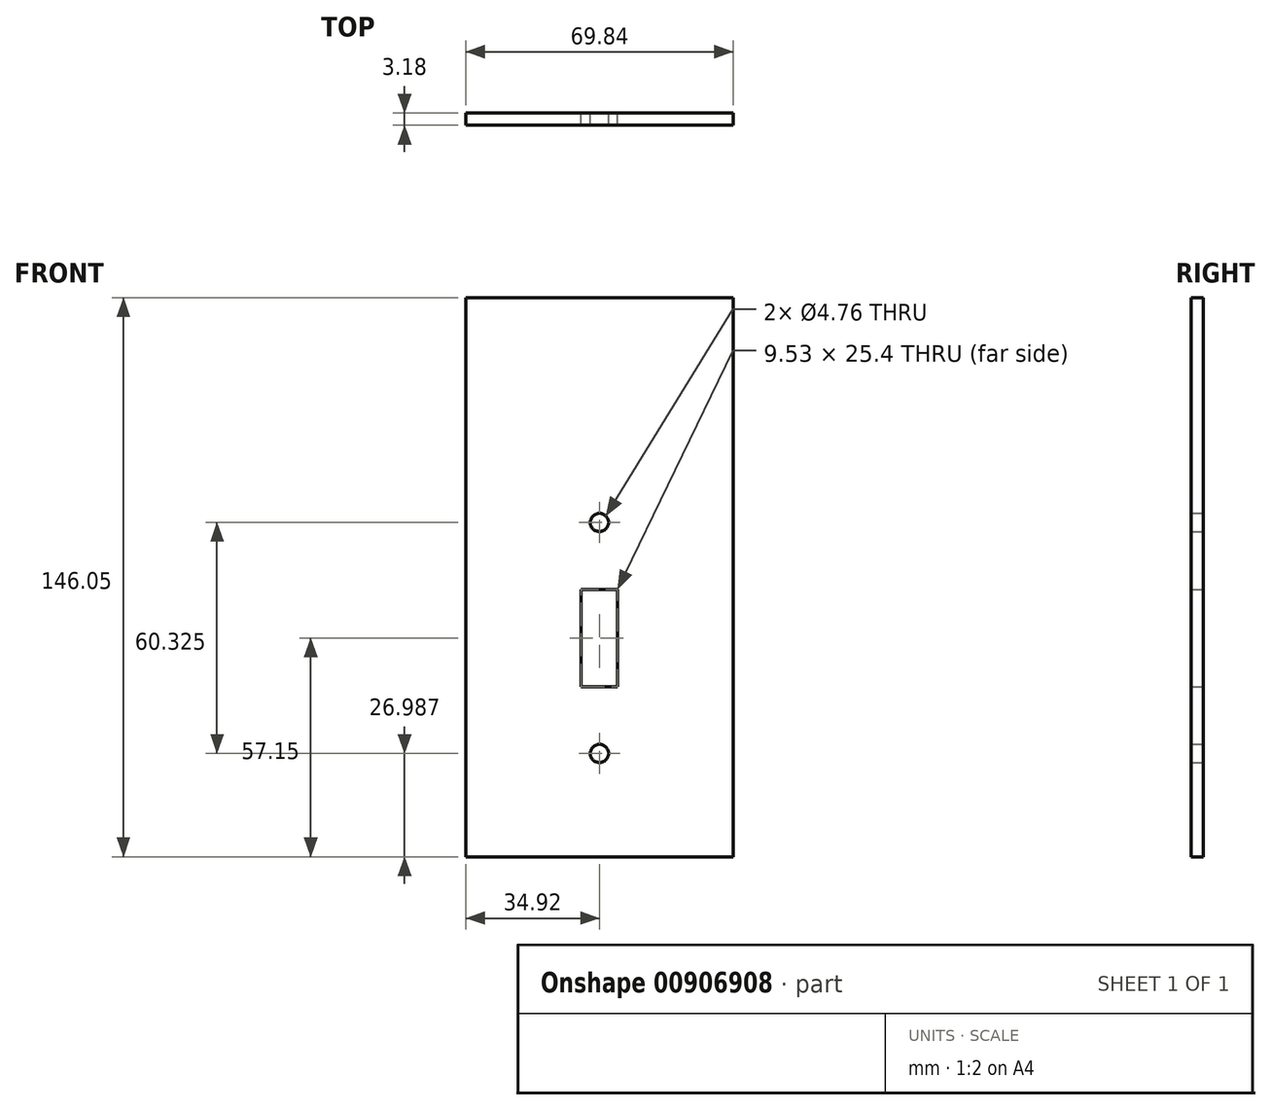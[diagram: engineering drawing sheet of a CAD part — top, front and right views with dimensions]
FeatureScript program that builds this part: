
annotation { "Feature Type Name" : "Feature", "Feature Type Description" : "" }
export const myFeature = defineFeature(function(context is Context, id is Id, definition is map)
    precondition{}
    {
        {
            var Q0;
            Q0=qCreatedBy(makeId("Front.planeOp"),FACE);
            var sketch = newSketch(context, id + "F0", { "sketchPlane" : qUnion([Q0])});
            skLineSegment(sketch, "E0.bottom", {"start": v(34.93, -57.15) * mm, "end": v(-34.92, -57.15) * mm});
            skLineSegment(sketch, "E0.top", {"start": v(34.92, 57.15) * mm, "end": v(-34.93, 57.15) * mm});
            skLineSegment(sketch, "E0.left", {"start": v(34.93, -57.15) * mm, "end": v(34.92, 57.15) * mm});
            skLineSegment(sketch, "E0.right", {"start": v(-34.92, -57.15) * mm, "end": v(-34.93, 57.15) * mm});
            skPoint(sketch, "E0.middle", {"position": v(0, 0) * mm});
            skLineSegment(sketch, "E1.bottom", {"start": v(4.76, -12.7) * mm, "end": v(-4.76, -12.7) * mm});
            skLineSegment(sketch, "E1.top", {"start": v(4.76, 12.7) * mm, "end": v(-4.76, 12.7) * mm});
            skLineSegment(sketch, "E1.left", {"start": v(4.76, -12.7) * mm, "end": v(4.76, 12.7) * mm});
            skLineSegment(sketch, "E1.right", {"start": v(-4.76, -12.7) * mm, "end": v(-4.76, 12.7) * mm});
            skCircle(sketch, "E2", {"center": v(0, 30.16) * mm, "radius": 2.38 * mm});
            skCircle(sketch, "E3", {"center": v(0, -30.16) * mm, "radius": 2.38 * mm});
            skLineSegment(sketch, "E4", {"start": v(0, 30.16) * mm, "end": v(0, -30.16) * mm, "construction": true});
            skLineSegment(sketch, "E5", {"start": v(-34.93, 57.15) * mm, "end": v(-34.93, 88.9) * mm});
            skLineSegment(sketch, "E6", {"start": v(-34.93, 88.9) * mm, "end": v(34.92, 88.9) * mm});
            skLineSegment(sketch, "E7", {"start": v(34.92, 88.9) * mm, "end": v(34.92, 57.15) * mm});
            skSolve(sketch);
        }
        {
            var Q0;
            Q0=makeQuery(id+"F0.imprint","IMPRINT",FACE,{"disambiguationData":[TD([[makeQuery(id+"F0.imprint","IMPRINT",EDGE,{"derivedFrom":sQuery(id+"F0.wireOp",EDGE,"E0.bottom")}),-1.0]])]});
            var Q1;
            Q1=makeQuery(id+"F0.imprint","IMPRINT",FACE,{"disambiguationData":[TD([[makeQuery(id+"F0.imprint","IMPRINT",EDGE,{"derivedFrom":sQuery(id+"F0.wireOp",EDGE,"E0.top")}),-1.0]])]});
            extrude(context, id + "F1", {"entities" : qUnion([Q0, Q1]), "depth" : 3.17 * mm, "offsetDistance" : 25.4 * mm});
        }
    });
